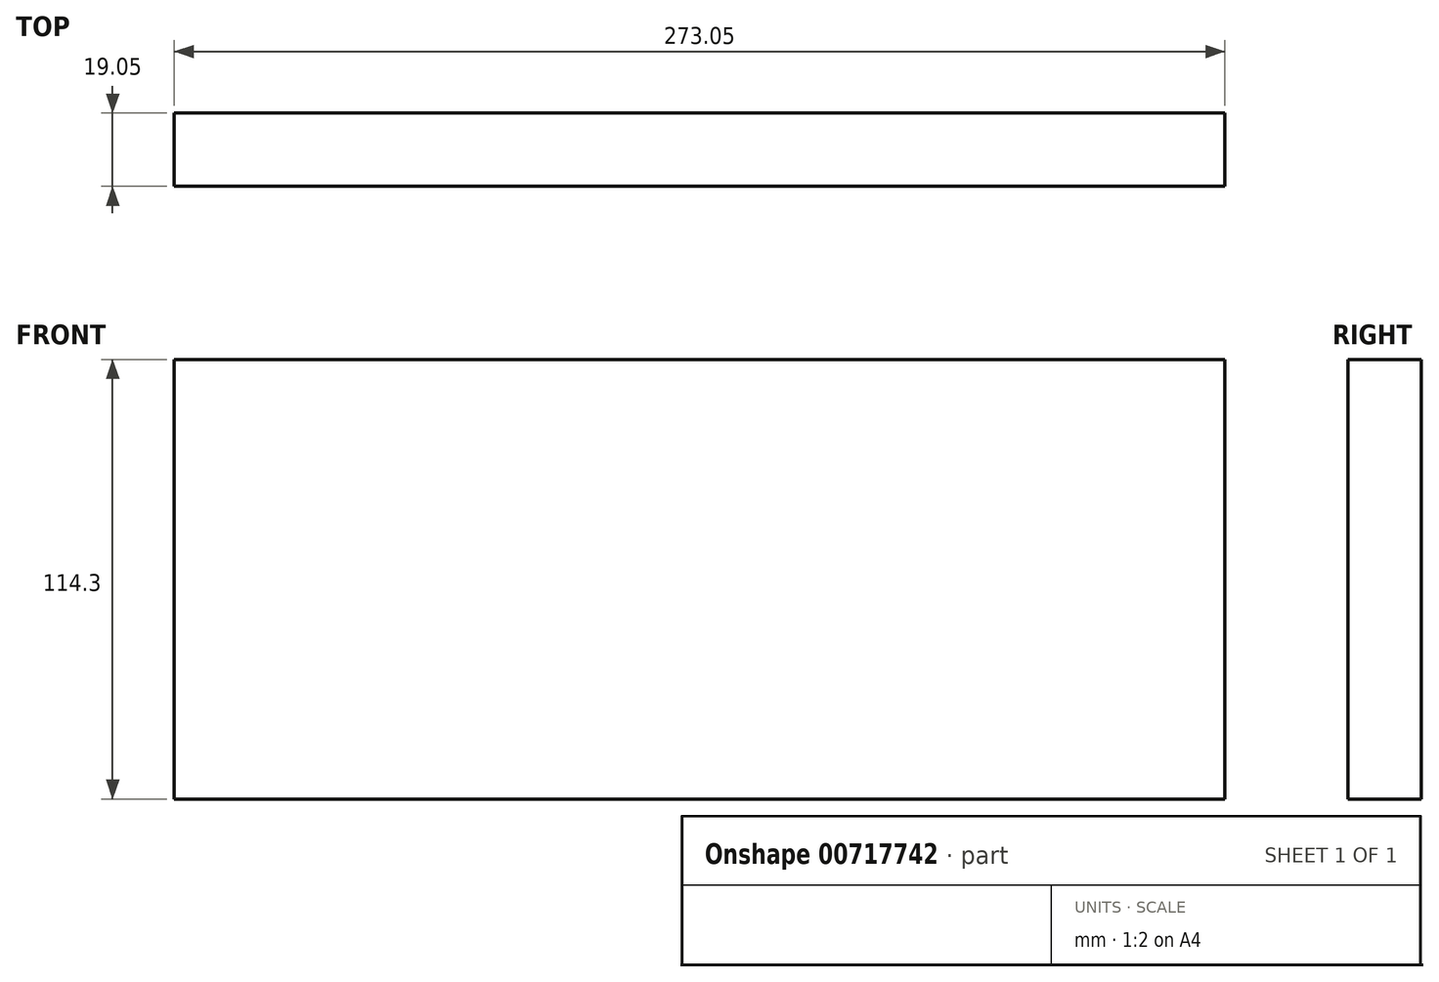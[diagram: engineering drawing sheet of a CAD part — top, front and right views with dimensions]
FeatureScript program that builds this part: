
annotation { "Feature Type Name" : "Feature", "Feature Type Description" : "" }
export const myFeature = defineFeature(function(context is Context, id is Id, definition is map)
    precondition{}
    {
        {
            var Q0;
            Q0=qCreatedBy(makeId("Front.planeOp"),FACE);
            var sketch = newSketch(context, id + "F0", { "sketchPlane" : qUnion([Q0])});
            skLineSegment(sketch, "E0.bottom", {"start": v(-87.36, 110.4) * mm, "end": v(185.7, 110.4) * mm});
            skLineSegment(sketch, "E0.top", {"start": v(-87.36, -3.9) * mm, "end": v(185.7, -3.9) * mm});
            skLineSegment(sketch, "E0.left", {"start": v(-87.36, 110.4) * mm, "end": v(-87.36, -3.9) * mm});
            skLineSegment(sketch, "E0.right", {"start": v(185.7, 110.4) * mm, "end": v(185.7, -3.9) * mm});
            skSolve(sketch);
        }
        {
            var Q0;
            Q0=makeQuery(id+"F0.imprint","IMPRINT",FACE,{"disambiguationData":[TD([[makeQuery(id+"F0.imprint","IMPRINT",EDGE,{"derivedFrom":sQuery(id+"F0.wireOp",EDGE,"E0.bottom")}),-1.0]])]});
            extrude(context, id + "F1", {"entities" : qUnion([Q0]), "depth" : 19.05 * mm, "offsetDistance" : 25.4 * mm});
        }
    });
